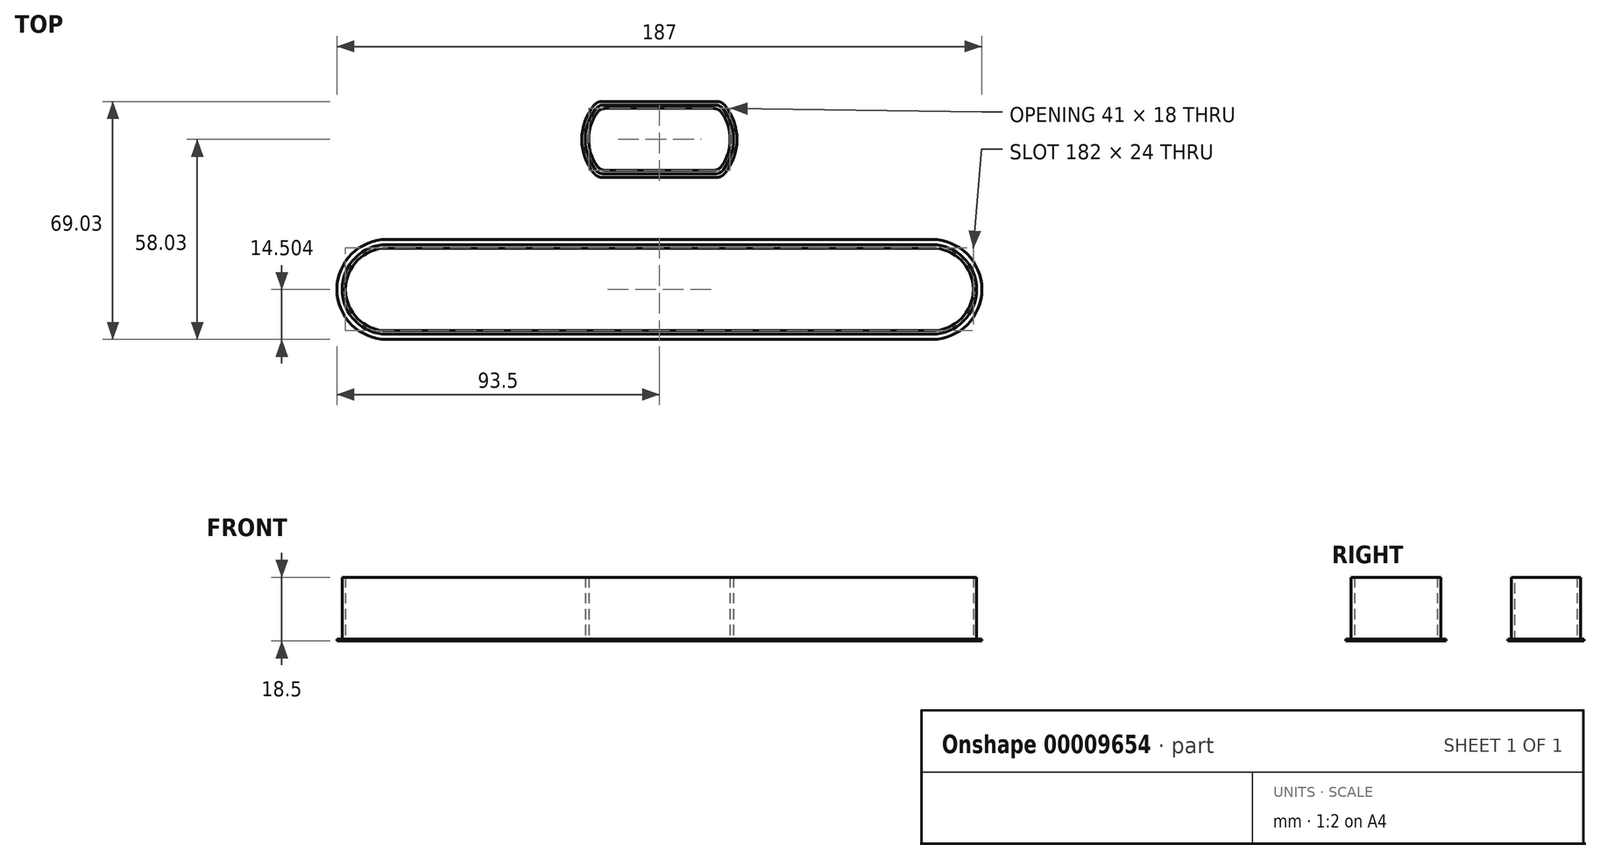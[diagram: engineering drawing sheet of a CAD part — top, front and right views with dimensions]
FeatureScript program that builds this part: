
annotation { "Feature Type Name" : "Feature", "Feature Type Description" : "" }
export const myFeature = defineFeature(function(context is Context, id is Id, definition is map)
    precondition{}
    {
        {
            var Q0;
            Q0=qCreatedBy(makeId("Top.planeOp"),FACE);
            var sketch = newSketch(context, id + "F0", { "sketchPlane" : qUnion([Q0])});
            skLineSegment(sketch, "E0.bottom", {"start": v(-17.5, 10) * mm, "end": v(17.5, 10) * mm});
            skLineSegment(sketch, "E0.top", {"start": v(-17.5, -10) * mm, "end": v(17.5, -10) * mm});
            skLineSegment(sketch, "E0.left", {"start": v(-17.5, 10) * mm, "end": v(-17.5, -10) * mm, "construction": true});
            skLineSegment(sketch, "E0.right", {"start": v(17.5, 10) * mm, "end": v(17.5, -10) * mm, "construction": true});
            skPoint(sketch, "E0.middle", {"position": v(0, 0) * mm});
            skArc(sketch, "E1", {"start": v(-17.5, 10) * mm, "mid": v(-21.5, 0) * mm, "end": v(-17.5, -10) * mm});
            skPoint(sketch, "E1.centerSnap0", {"position": v(-17.5, 0) * mm});
            skPoint(sketch, "E2", {"position": v(-21.5, 0) * mm});
            skArc(sketch, "E3.MirrorCS", {"start": v(17.5, 10) * mm, "mid": v(21.5, 0) * mm, "end": v(17.5, -10) * mm});
            skLineSegment(sketch, "E4.0", {"start": v(-17.06, 9) * mm, "end": v(17.06, 9) * mm});
            skArc(sketch, "E4.1", {"start": v(-17.06, 9) * mm, "mid": v(-20.5, 0) * mm, "end": v(-17.06, -9) * mm});
            skLineSegment(sketch, "E4.2", {"start": v(-17.06, -9) * mm, "end": v(17.06, -9) * mm});
            skArc(sketch, "E4.3", {"start": v(17.06, 9) * mm, "mid": v(20.5, 0) * mm, "end": v(17.06, -9) * mm});
            skLineSegment(sketch, "E5.bottom", {"start": v(-79, -30.53) * mm, "end": v(79, -30.53) * mm});
            skLineSegment(sketch, "E5.top", {"start": v(-79, -56.53) * mm, "end": v(79, -56.53) * mm});
            skLineSegment(sketch, "E5.left", {"start": v(-79, -30.53) * mm, "end": v(-79, -56.53) * mm, "construction": true});
            skLineSegment(sketch, "E5.right", {"start": v(79, -30.53) * mm, "end": v(79, -56.53) * mm, "construction": true});
            skPoint(sketch, "E5.middle", {"position": v(0, -43.53) * mm});
            skArc(sketch, "E6", {"start": v(-79, -30.53) * mm, "mid": v(-92, -43.53) * mm, "end": v(-79, -56.53) * mm});
            skPoint(sketch, "E6.centerSnap0", {"position": v(-79, -43.53) * mm});
            skPoint(sketch, "E7", {"position": v(-92, -43.53) * mm});
            skArc(sketch, "E8.MirrorCS", {"start": v(79, -30.53) * mm, "mid": v(92, -43.53) * mm, "end": v(79, -56.53) * mm});
            skArc(sketch, "E9.0", {"start": v(-79, -31.53) * mm, "mid": v(-91, -43.53) * mm, "end": v(-79, -55.53) * mm});
            skLineSegment(sketch, "E9.1", {"start": v(-79, -31.53) * mm, "end": v(79, -31.53) * mm});
            skArc(sketch, "E9.2", {"start": v(79, -31.53) * mm, "mid": v(91, -43.53) * mm, "end": v(79, -55.53) * mm});
            skLineSegment(sketch, "E9.3", {"start": v(-79, -55.53) * mm, "end": v(79, -55.53) * mm});
            skPoint(sketch, "E10", {"position": v(92, -43.53) * mm});
            skSolve(sketch);
        }
        {
            var Q0;
            Q0 = qSketchRegion(id + "F0", true);
            extrude(context, id + "F1", {"entities" : qUnion([Q0]), "depth" : 18 * mm, "offsetDistance" : 25 * mm});
        }
        {
            var Q0;
            Q0=makeQuery(id+"F1.opExtrude","CAP_FACE",FACE,{"disambiguationData":[OSD([sQuery(id+"F0.wireOp",EDGE,"E0.bottom"),sQuery(id+"F0.wireOp",EDGE,"E0.top"),sQuery(id+"F0.wireOp",EDGE,"E1"),sQuery(id+"F0.wireOp",EDGE,"E3.MirrorCS"),sQuery(id+"F0.wireOp",EDGE,"E4.0"),sQuery(id+"F0.wireOp",EDGE,"E4.1"),sQuery(id+"F0.wireOp",EDGE,"E4.2"),sQuery(id+"F0.wireOp",EDGE,"E4.3")])],"isStart":true});
            var sketch = newSketch(context, id + "F2", { "sketchPlane" : qUnion([Q0])});
            skLineSegment(sketch, "E11.0", {"start": v(-17.92, 11) * mm, "end": v(17.92, 11) * mm});
            skArc(sketch, "E11.1", {"start": v(-17.92, -11) * mm, "mid": v(-22.5, 0) * mm, "end": v(-17.92, 11) * mm});
            skLineSegment(sketch, "E11.2", {"start": v(-17.92, -11) * mm, "end": v(17.92, -11) * mm});
            skArc(sketch, "E11.3", {"start": v(17.92, -11) * mm, "mid": v(22.5, 0) * mm, "end": v(17.92, 11) * mm});
            skLineSegment(sketch, "E12.0", {"start": v(-17.06, 9) * mm, "end": v(17.06, 9) * mm});
            skArc(sketch, "E13.0", {"start": v(-17.06, -9) * mm, "mid": v(-20.5, 0) * mm, "end": v(-17.06, 9) * mm});
            skLineSegment(sketch, "E14.0", {"start": v(-17.06, -9) * mm, "end": v(17.06, -9) * mm});
            skArc(sketch, "E15.0", {"start": v(17.06, -9) * mm, "mid": v(20.5, 0) * mm, "end": v(17.06, 9) * mm});
            skLineSegment(sketch, "E16.0", {"start": v(-79, 55.53) * mm, "end": v(79, 55.53) * mm});
            skArc(sketch, "E17.0", {"start": v(-79, 31.53) * mm, "mid": v(-91, 43.53) * mm, "end": v(-79, 55.53) * mm});
            skLineSegment(sketch, "E18.0", {"start": v(-79, 31.53) * mm, "end": v(79, 31.53) * mm});
            skArc(sketch, "E19.0", {"start": v(79, 31.53) * mm, "mid": v(91, 43.53) * mm, "end": v(79, 55.53) * mm});
            skArc(sketch, "E20.0", {"start": v(79, 29.03) * mm, "mid": v(93.5, 43.53) * mm, "end": v(79, 58.03) * mm});
            skLineSegment(sketch, "E20.1", {"start": v(-79, 29.03) * mm, "end": v(79, 29.03) * mm});
            skArc(sketch, "E20.2", {"start": v(-79, 29.03) * mm, "mid": v(-93.5, 43.53) * mm, "end": v(-79, 58.03) * mm});
            skLineSegment(sketch, "E20.3", {"start": v(-79, 58.03) * mm, "end": v(79, 58.03) * mm});
            skSolve(sketch);
        }
        {
            var Q0;
            Q0 = qSketchRegion(id + "F2", true);
            extrude(context, id + "F3", {"entities" : qUnion([Q0]), "operationType" : NewBodyOperationType.ADD, "depth" : .5 * mm, "offsetDistance" : 25 * mm});
        }
        {
            var Q0;
            Q0=makeQuery(id+"F3.boolean.opBoolean","MERGE",EDGE,{"derivedFrom":[makeQuery(id+"F1.opExtrude","SWEPT_EDGE",EDGE,{"disambiguationData":[OSD([sQuery(id+"F0.wireOp",EDGE,"E4.1"),sQuery(id+"F0.wireOp",EDGE,"E4.2")])]}),makeQuery(id+"F3.opExtrude","SWEPT_EDGE",EDGE,{"disambiguationData":[OSD([sQuery(id+"F2.wireOp",EDGE,"E12.0"),sQuery(id+"F2.wireOp",EDGE,"E13.0")])]})]});
            var Q1;
            Q1=makeQuery(id+"F3.boolean.opBoolean","MERGE",EDGE,{"derivedFrom":[makeQuery(id+"F1.opExtrude","SWEPT_EDGE",EDGE,{"disambiguationData":[OSD([sQuery(id+"F0.wireOp",EDGE,"E4.2"),sQuery(id+"F0.wireOp",EDGE,"E4.3")])]}),makeQuery(id+"F3.opExtrude","SWEPT_EDGE",EDGE,{"disambiguationData":[OSD([sQuery(id+"F2.wireOp",EDGE,"E12.0"),sQuery(id+"F2.wireOp",EDGE,"E15.0")])]})]});
            var Q2;
            Q2=makeQuery(id+"F3.boolean.opBoolean","MERGE",EDGE,{"derivedFrom":[makeQuery(id+"F1.opExtrude","SWEPT_EDGE",EDGE,{"disambiguationData":[OSD([sQuery(id+"F0.wireOp",EDGE,"E4.0"),sQuery(id+"F0.wireOp",EDGE,"E4.3")])]}),makeQuery(id+"F3.opExtrude","SWEPT_EDGE",EDGE,{"disambiguationData":[OSD([sQuery(id+"F2.wireOp",EDGE,"E14.0"),sQuery(id+"F2.wireOp",EDGE,"E15.0")])]})]});
            var Q3;
            Q3=makeQuery(id+"F3.boolean.opBoolean","MERGE",EDGE,{"derivedFrom":[makeQuery(id+"F1.opExtrude","SWEPT_EDGE",EDGE,{"disambiguationData":[OSD([sQuery(id+"F0.wireOp",EDGE,"E4.0"),sQuery(id+"F0.wireOp",EDGE,"E4.1")])]}),makeQuery(id+"F3.opExtrude","SWEPT_EDGE",EDGE,{"disambiguationData":[OSD([sQuery(id+"F2.wireOp",EDGE,"E13.0"),sQuery(id+"F2.wireOp",EDGE,"E14.0")])]})]});
            var Q4;
            Q4=makeQuery(id+"F1.opExtrude","SWEPT_EDGE",EDGE,{"disambiguationData":[OSD([sQuery(id+"F0.wireOp",EDGE,"E0.top"),sQuery(id+"F0.wireOp",EDGE,"E1")])]});
            var Q5;
            Q5=makeQuery(id+"F1.opExtrude","SWEPT_EDGE",EDGE,{"disambiguationData":[OSD([sQuery(id+"F0.wireOp",EDGE,"E0.top"),sQuery(id+"F0.wireOp",EDGE,"E3.MirrorCS")])]});
            var Q6;
            Q6=makeQuery(id+"F1.opExtrude","SWEPT_EDGE",EDGE,{"disambiguationData":[OSD([sQuery(id+"F0.wireOp",EDGE,"E0.bottom"),sQuery(id+"F0.wireOp",EDGE,"E3.MirrorCS")])]});
            var Q7;
            Q7=makeQuery(id+"F1.opExtrude","SWEPT_EDGE",EDGE,{"disambiguationData":[OSD([sQuery(id+"F0.wireOp",EDGE,"E0.bottom"),sQuery(id+"F0.wireOp",EDGE,"E1")])]});
            var Q8;
            Q8=makeQuery(id+"F3.opExtrude","SWEPT_EDGE",EDGE,{"disambiguationData":[OSD([sQuery(id+"F2.wireOp",EDGE,"E11.0"),sQuery(id+"F2.wireOp",EDGE,"E11.3")])]});
            var Q9;
            Q9=makeQuery(id+"F3.opExtrude","SWEPT_EDGE",EDGE,{"disambiguationData":[OSD([sQuery(id+"F2.wireOp",EDGE,"E11.2"),sQuery(id+"F2.wireOp",EDGE,"E11.3")])]});
            var Q10;
            Q10=makeQuery(id+"F3.opExtrude","SWEPT_EDGE",EDGE,{"disambiguationData":[OSD([sQuery(id+"F2.wireOp",EDGE,"E11.1"),sQuery(id+"F2.wireOp",EDGE,"E11.2")])]});
            var Q11;
            Q11=makeQuery(id+"F3.opExtrude","SWEPT_EDGE",EDGE,{"disambiguationData":[OSD([sQuery(id+"F2.wireOp",EDGE,"E11.0"),sQuery(id+"F2.wireOp",EDGE,"E11.1")])]});
            fillet(context, id + "F4", {"entities" : qUnion([Q0, Q1, Q2, Q3, Q4, Q5, Q6, Q7, Q8, Q9, Q10, Q11]), "tangentPropagation" : true, "radius" : 3 * mm, "defaultsChanged" : false, "vertexSettings" : [], "allowEdgeOverflow" : false});
        }
    });
